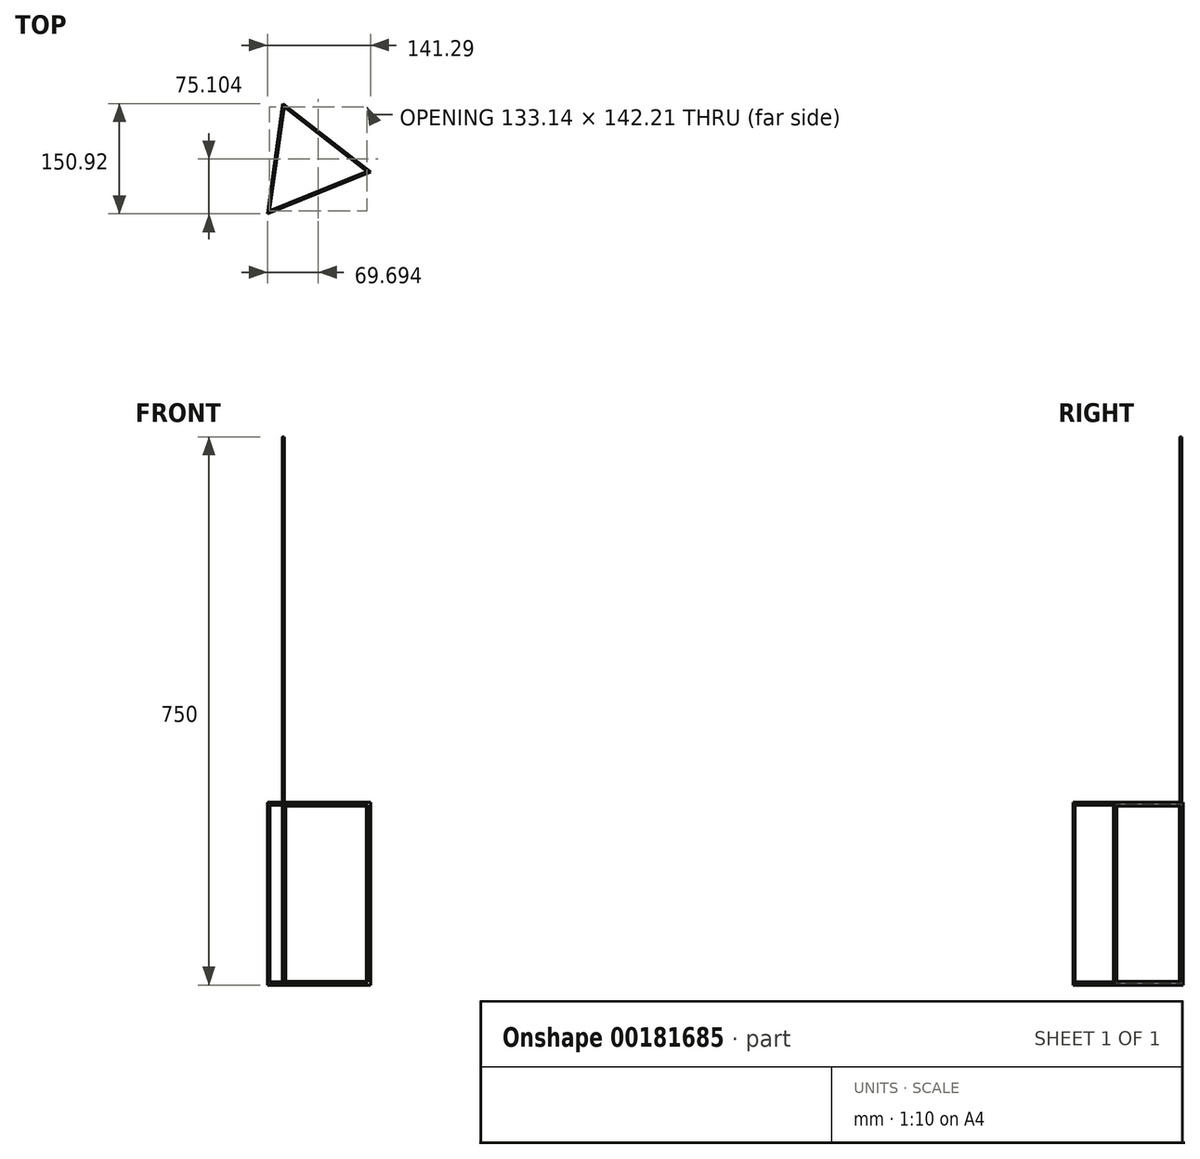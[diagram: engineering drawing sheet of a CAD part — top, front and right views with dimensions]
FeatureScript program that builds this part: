
annotation { "Feature Type Name" : "Feature", "Feature Type Description" : "" }
export const myFeature = defineFeature(function(context is Context, id is Id, definition is map)
    precondition{}
    {
        {
            var Q0;
            Q0=qCreatedBy(makeId("Top.planeOp"),FACE);
            var sketch = newSketch(context, id + "F0", { "sketchPlane" : qUnion([Q0])});
            skCircle(sketch, "E0.cCircle", {"center": v(0, 0) * mm, "radius": 44 * mm, "construction": true});
            skLineSegment(sketch, "E0.0", {"start": v(-32.97, 81.58) * mm, "end": v(87.13, -12.24) * mm});
            skLineSegment(sketch, "E0.1", {"start": v(87.13, -12.24) * mm, "end": v(-54.16, -69.34) * mm});
            skLineSegment(sketch, "E0.2", {"start": v(-54.16, -69.34) * mm, "end": v(-32.97, 81.58) * mm});
            skPoint(sketch, "E0.0.midPoint", {"position": v(27.08, 34.67) * mm});
            skSolve(sketch);
        }
        {
            var Q0;
            Q0=makeQuery(id+"F0.imprint","IMPRINT",FACE,{"disambiguationData":[TD([[makeQuery(id+"F0.imprint","IMPRINT",EDGE,{"derivedFrom":sQuery(id+"F0.wireOp",EDGE,"E0.0")}),-1.0]])]});
            extrude(context, id + "F1", {"entities" : qUnion([Q0]), "oppositeDirection" : true, "depth" : 250 * mm});
        }
        {
            var Q0;
            Q0=makeQuery(id+"F1.opExtrude","CAP_FACE",FACE,{"disambiguationData":[OSD([sQuery(id+"F0.wireOp",EDGE,"E0.0"),sQuery(id+"F0.wireOp",EDGE,"E0.1"),sQuery(id+"F0.wireOp",EDGE,"E0.2")])],"isStart":true});
            var sketch = newSketch(context, id + "F2", { "sketchPlane" : qUnion([Q0])});
            skLineSegment(sketch, "E1.0.0", {"start": v(87.13, -12.24) * mm, "end": v(-32.97, 81.58) * mm});
            skLineSegment(sketch, "E1.0.1", {"start": v(-32.97, 81.58) * mm, "end": v(-54.16, -69.34) * mm});
            skLineSegment(sketch, "E1.0.2", {"start": v(-54.16, -69.34) * mm, "end": v(87.13, -12.24) * mm});
            skLineSegment(sketch, "E2.0", {"start": v(82.1, -11.53) * mm, "end": v(-31.07, 76.87) * mm});
            skLineSegment(sketch, "E2.1", {"start": v(-51.04, -65.34) * mm, "end": v(82.1, -11.53) * mm});
            skLineSegment(sketch, "E2.2", {"start": v(-31.07, 76.87) * mm, "end": v(-51.04, -65.34) * mm});
            skSolve(sketch);
        }
        {
            var Q0;
            Q0=makeQuery(id+"F2.imprint","IMPRINT",FACE,{"disambiguationData":[TD([[makeQuery(id+"F2.imprint","IMPRINT",EDGE,{"derivedFrom":sQuery(id+"F2.wireOp",EDGE,"E2.0")}),1.0]])]});
            extrude(context, id + "F3", {"entities" : qUnion([Q0]), "operationType" : NewBodyOperationType.REMOVE, "endBound" : BoundingType.UP_TO_NEXT, "oppositeDirection" : true, "depth" : 25.4 * mm});
        }
        {
            var Q0;
            Q0=makeQuery(id+"F1.opExtrude","SWEPT_FACE",FACE,{"disambiguationData":[OSD([sQuery(id+"F0.wireOp",EDGE,"E0.0")])]});
            var sketch = newSketch(context, id + "F4", { "sketchPlane" : qUnion([Q0])});
            skLineSegment(sketch, "E3.0", {"start": v(71.2, -5) * mm, "end": v(-71.2, -5) * mm});
            skLineSegment(sketch, "E3.1", {"start": v(71.2, -245) * mm, "end": v(71.2, -5) * mm});
            skLineSegment(sketch, "E3.2", {"start": v(71.2, -245) * mm, "end": v(-71.2, -245) * mm});
            skLineSegment(sketch, "E3.3", {"start": v(-71.2, -245) * mm, "end": v(-71.2, -5) * mm});
            skSolve(sketch);
        }
        {
            var Q0;
            Q0=makeQuery(id+"F4.imprint","IMPRINT",FACE,{"disambiguationData":[TD([[makeQuery(id+"F4.imprint","IMPRINT",EDGE,{"derivedFrom":sQuery(id+"F4.wireOp",EDGE,"E3.0")}),1.0]])]});
            extrude(context, id + "F5", {"entities" : qUnion([Q0]), "operationType" : NewBodyOperationType.REMOVE, "endBound" : BoundingType.UP_TO_NEXT, "oppositeDirection" : true, "depth" : 25.4 * mm});
        }
        {
            var Q0;
            Q0=makeQuery(id+"F1.opExtrude","SWEPT_FACE",FACE,{"disambiguationData":[OSD([sQuery(id+"F0.wireOp",EDGE,"E0.2")])]});
            var sketch = newSketch(context, id + "F6", { "sketchPlane" : qUnion([Q0])});
            skLineSegment(sketch, "E4.0", {"start": v(73.2, -3) * mm, "end": v(-73.2, -3) * mm});
            skLineSegment(sketch, "E4.1", {"start": v(73.2, -247) * mm, "end": v(73.2, -3) * mm});
            skLineSegment(sketch, "E4.2", {"start": v(73.2, -247) * mm, "end": v(-73.2, -247) * mm});
            skLineSegment(sketch, "E4.3", {"start": v(-73.2, -247) * mm, "end": v(-73.2, -3) * mm});
            skSolve(sketch);
        }
        {
            var Q0;
            Q0=makeQuery(id+"F6.imprint","IMPRINT",FACE,{"disambiguationData":[TD([[makeQuery(id+"F6.imprint","IMPRINT",EDGE,{"derivedFrom":sQuery(id+"F6.wireOp",EDGE,"E4.0")}),1.0]])]});
            extrude(context, id + "F7", {"entities" : qUnion([Q0]), "operationType" : NewBodyOperationType.REMOVE, "oppositeDirection" : true, "depth" : 3 * mm});
        }
        {
            var Q0;
            Q0=makeQuery(id+"F1.opExtrude","SWEPT_FACE",FACE,{"disambiguationData":[OSD([sQuery(id+"F0.wireOp",EDGE,"E0.1")])]});
            var sketch = newSketch(context, id + "F8", { "sketchPlane" : qUnion([Q0])});
            skSolve(sketch);
        }
        {
            var Q0;
            {var subQ0=sQuery(id+"F0.wireOp",EDGE,"E0.1");Q0=makeQuery(id+"F8.imprint","IMPRINT",FACE,{"disambiguationData":[TD([[makeQuery(id+"F8.imprint","IMPRINT",EDGE,{"derivedFrom":makeQuery(id+"F1.opExtrude","CAP_EDGE",EDGE,{"disambiguationData":[OSD([subQ0])],"isStart":true})}),1.0]])]});}
            var sketch = newSketch(context, id + "F9", { "sketchPlane" : qUnion([Q0])});
            skLineSegment(sketch, "E5.0", {"start": v(72.2, -4) * mm, "end": v(-72.2, -4) * mm});
            skLineSegment(sketch, "E5.1", {"start": v(72.2, -246) * mm, "end": v(72.2, -4) * mm});
            skLineSegment(sketch, "E5.2", {"start": v(72.2, -246) * mm, "end": v(-72.2, -246) * mm});
            skLineSegment(sketch, "E5.3", {"start": v(-72.2, -246) * mm, "end": v(-72.2, -4) * mm});
            skSolve(sketch);
        }
        {
            var Q0;
            Q0 = qSketchRegion(id + "F9", true);
            var Q1;
            {var subQ0=sQuery(id+"F0.wireOp",EDGE,"E0.1");Q1=makeQuery(id+"F8.imprint","IMPRINT",FACE,{"disambiguationData":[TD([[makeQuery(id+"F8.imprint","IMPRINT",EDGE,{"derivedFrom":makeQuery(id+"F1.opExtrude","CAP_EDGE",EDGE,{"disambiguationData":[OSD([subQ0])],"isStart":true})}),1.0]])]});}
            extrude(context, id + "F10", {"entities" : qUnion([Q0, Q1]), "operationType" : NewBodyOperationType.ADD, "depth" : 3 * mm});
        }
        {
            var Q0;
            Q0 = qSketchRegion(id + "F9", true);
            var Q1;
            Q1=makeQuery(id+"F10.opExtrude","CAP_FACE",FACE,{"disambiguationData":[OSD([sQuery(id+"F0.wireOp",EDGE,"E0.0"),sQuery(id+"F0.wireOp",EDGE,"E0.1"),sQuery(id+"F0.wireOp",EDGE,"E0.2")])],"isStart":false});
            extrude(context, id + "F11", {"entities" : qUnion([Q0, Q1]), "operationType" : NewBodyOperationType.REMOVE, "oppositeDirection" : true, "depth" : 3 * mm});
        }
        {
            var Q0;
            {var subQ0=sQuery(id+"F0.wireOp",EDGE,"E0.1");Q0=makeQuery(id+"F10.boolean.opBoolean","MERGE",FACE,{"derivedFrom":[makeQuery(id+"F1.opExtrude","CAP_FACE",FACE,{"disambiguationData":[OSD([sQuery(id+"F0.wireOp",EDGE,"E0.0"),subQ0,sQuery(id+"F0.wireOp",EDGE,"E0.2")])],"isStart":true}),makeQuery(id+"F10.opExtrude","SWEPT_FACE",FACE,{"disambiguationData":[OSD([subQ0]),TDD([makeQuery(id+"F8.imprint","IMPRINT",EDGE,{"derivedFrom":makeQuery(id+"F1.opExtrude","CAP_EDGE",EDGE,{"disambiguationData":[OSD([subQ0])],"isStart":true})})])]})]});}
            var sketch = newSketch(context, id + "F12", { "sketchPlane" : qUnion([Q0])});
            skCircle(sketch, "E6", {"center": v(-32.13, 78.45) * mm, "radius": 1.27 * mm});
            skSolve(sketch);
        }
        {
            var Q0;
            Q0 = qSketchRegion(id + "F12", true);
            extrude(context, id + "F13", {"entities" : qUnion([Q0]), "operationType" : NewBodyOperationType.ADD, "depth" : 500 * mm});
        }
    });
